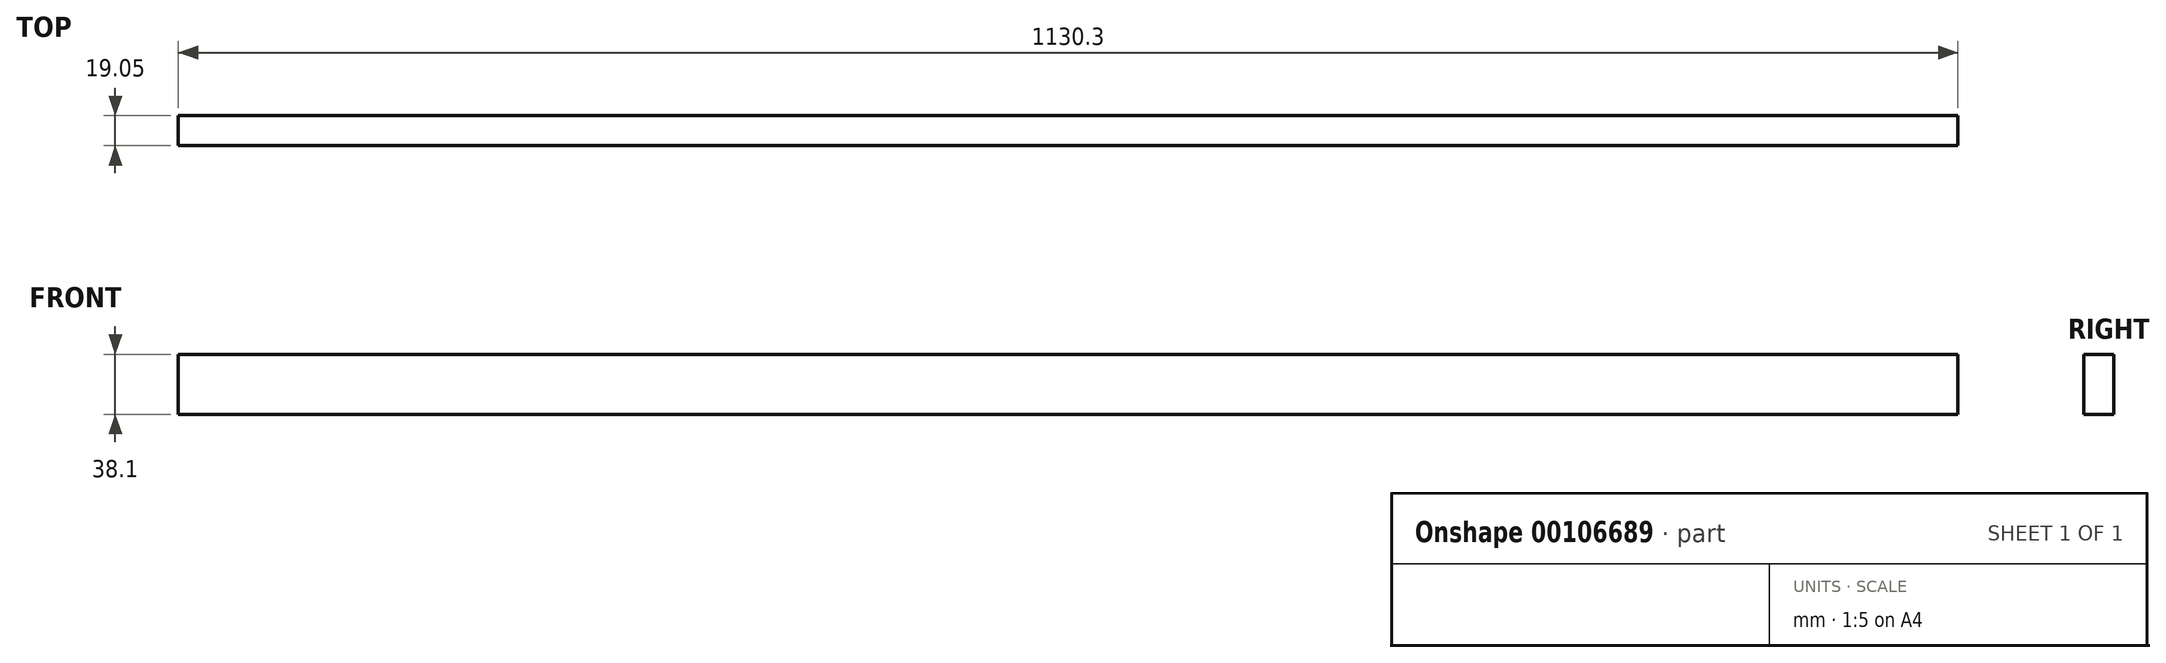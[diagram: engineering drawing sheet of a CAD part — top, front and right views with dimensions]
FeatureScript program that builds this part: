
annotation { "Feature Type Name" : "Feature", "Feature Type Description" : "" }
export const myFeature = defineFeature(function(context is Context, id is Id, definition is map)
    precondition{}
    {
        {
            var Q0;
            Q0=qCreatedBy(makeId("Front.planeOp"),FACE);
            var sketch = newSketch(context, id + "F0", { "sketchPlane" : qUnion([Q0])});
            skLineSegment(sketch, "E0.bottom", {"start": v(0, 0) * mm, "end": v(1130.3, 0) * mm});
            skLineSegment(sketch, "E0.top", {"start": v(0, 38.1) * mm, "end": v(1130.3, 38.1) * mm});
            skLineSegment(sketch, "E0.left", {"start": v(0, 0) * mm, "end": v(0, 38.1) * mm});
            skLineSegment(sketch, "E0.right", {"start": v(1130.3, 0) * mm, "end": v(1130.3, 38.1) * mm});
            skSolve(sketch);
        }
        {
            var Q0;
            Q0=makeQuery(id+"F0.imprint","IMPRINT",FACE,{"disambiguationData":[TD([[makeQuery(id+"F0.imprint","IMPRINT",EDGE,{"derivedFrom":sQuery(id+"F0.wireOp",EDGE,"E0.bottom")}),1.0]])]});
            extrude(context, id + "F1", {"entities" : qUnion([Q0]), "depth" : 19.05 * mm});
        }
    });
